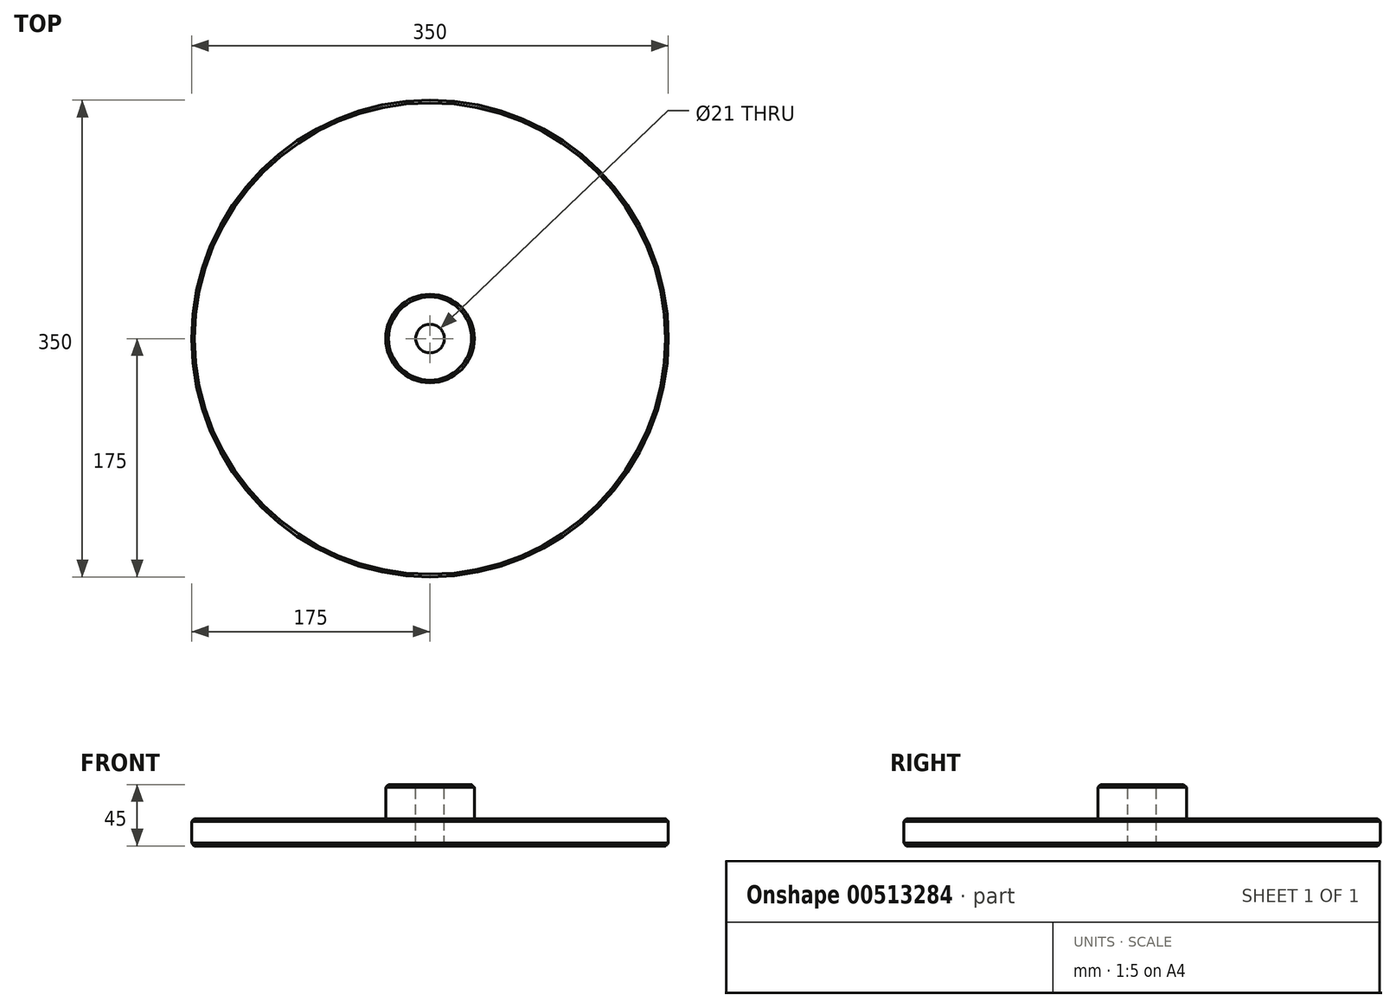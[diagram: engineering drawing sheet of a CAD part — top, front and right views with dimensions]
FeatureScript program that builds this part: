
annotation { "Feature Type Name" : "Feature", "Feature Type Description" : "" }
export const myFeature = defineFeature(function(context is Context, id is Id, definition is map)
    precondition{}
    {
        {
            var Q0;
            Q0=qCreatedBy(makeId("Top.planeOp"),FACE);
            var sketch = newSketch(context, id + "F0", { "sketchPlane" : qUnion([Q0])});
            skCircle(sketch, "E0", {"center": v(0, 0) * mm, "radius": 175 * mm});
            skCircle(sketch, "E1", {"center": v(0, 0) * mm, "radius": 32.5 * mm});
            skCircle(sketch, "E2", {"center": v(0, 0) * mm, "radius": 10.5 * mm});
            skSolve(sketch);
        }
        {
            var Q0;
            Q0=makeQuery(id+"F0.imprint","IMPRINT",FACE,{"disambiguationData":[TD([[makeQuery(id+"F0.imprint","IMPRINT",EDGE,{"derivedFrom":sQuery(id+"F0.wireOp",EDGE,"E0")}),1.0]])]});
            var Q1;
            Q1=makeQuery(id+"F0.imprint","IMPRINT",FACE,{"disambiguationData":[TD([[makeQuery(id+"F0.imprint","IMPRINT",EDGE,{"derivedFrom":sQuery(id+"F0.wireOp",EDGE,"E1")}),1.0]])]});
            extrude(context, id + "F1", {"entities" : qUnion([Q0, Q1]), "oppositeDirection" : true, "depth" : 20 * mm});
        }
        {
            var Q0;
            Q0=makeQuery(id+"F0.imprint","IMPRINT",FACE,{"disambiguationData":[TD([[makeQuery(id+"F0.imprint","IMPRINT",EDGE,{"derivedFrom":sQuery(id+"F0.wireOp",EDGE,"E1")}),1.0]])]});
            extrude(context, id + "F2", {"entities" : qUnion([Q0]), "operationType" : NewBodyOperationType.ADD, "depth" : 25 * mm});
        }
        {
            var Q0;
            Q0=makeQuery(id+"F1.opExtrude","CAP_EDGE",EDGE,{"disambiguationData":[OSD([sQuery(id+"F0.wireOp",EDGE,"E0")])],"isStart":true});
            var Q1;
            Q1=makeQuery(id+"F1.opExtrude","CAP_EDGE",EDGE,{"disambiguationData":[OSD([sQuery(id+"F0.wireOp",EDGE,"E0")])],"isStart":false});
            var Q2;
            Q2=makeQuery(id+"F2.opExtrude","CAP_EDGE",EDGE,{"disambiguationData":[OSD([sQuery(id+"F0.wireOp",EDGE,"E1")])],"isStart":false});
            chamfer(context, id + "F3", {"entities" : qUnion([Q0, Q1, Q2]), "width" : 2 * mm, "tangentPropagation" : true});
        }
    });
